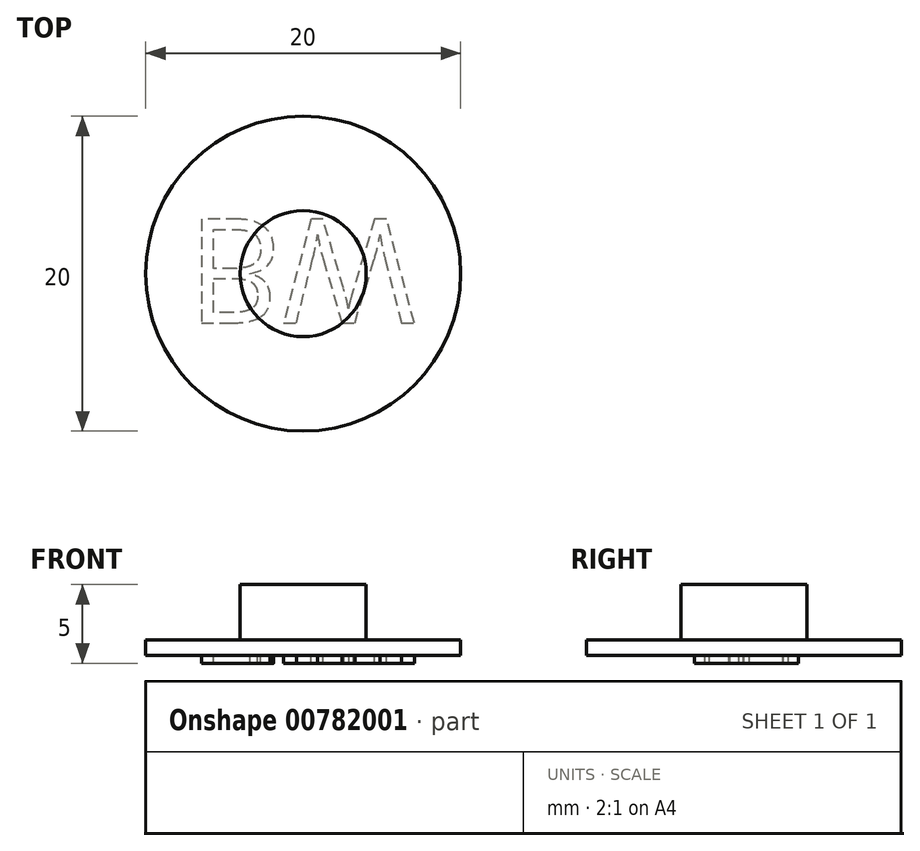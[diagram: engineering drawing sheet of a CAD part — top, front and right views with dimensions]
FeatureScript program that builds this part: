
annotation { "Feature Type Name" : "Feature", "Feature Type Description" : "" }
export const myFeature = defineFeature(function(context is Context, id is Id, definition is map)
    precondition{}
    {
        {
            var Q0;
            Q0=qCreatedBy(makeId("Top.planeOp"),FACE);
            var sketch = newSketch(context, id + "F0", { "sketchPlane" : qUnion([Q0])});
            skCircle(sketch, "E0", {"center": v(0, 0) * mm, "radius": 10 * mm});
            skSolve(sketch);
        }
        {
            var Q0;
            Q0=makeQuery(id+"F0.imprint","IMPRINT",FACE,{"disambiguationData":[TD([[makeQuery(id+"F0.imprint","IMPRINT",EDGE,{"derivedFrom":sQuery(id+"F0.wireOp",EDGE,"E0")}),1.0]])]});
            extrude(context, id + "F1", {"entities" : qUnion([Q0]), "depth" : 1 * mm, "offsetDistance" : 25.4 * mm});
        }
        {
            var Q0;
            Q0=makeQuery(id+"F1.opExtrude","CAP_FACE",FACE,{"disambiguationData":[OSD([sQuery(id+"F0.wireOp",EDGE,"E0")])],"isStart":false});
            var sketch = newSketch(context, id + "F2", { "sketchPlane" : qUnion([Q0])});
            skCircle(sketch, "E1", {"center": v(0, 0) * mm, "radius": 4 * mm});
            skSolve(sketch);
        }
        {
            var Q0;
            Q0 = qSketchRegion(id + "F2", true);
            extrude(context, id + "F3", {"entities" : qUnion([Q0]), "operationType" : NewBodyOperationType.ADD, "depth" : 3.5 * mm, "offsetDistance" : 25.4 * mm});
        }
        {
            var Q0;
            Q0=makeQuery(id+"F1.opExtrude","CAP_FACE",FACE,{"disambiguationData":[OSD([sQuery(id+"F0.wireOp",EDGE,"E0")])],"isStart":true});
            var sketch = newSketch(context, id + "F4", { "sketchPlane" : qUnion([Q0])});
            skText(sketch, "E2", { "text": "BW", "fontName": "OpenSans-Regular.ttf"});
            const initialGuessF4  = {"E2": [-0.00735, -0.00346, 1, 0, 0.00665]};
            skSetInitialGuess(sketch, initialGuessF4);
            skSolve(sketch);
        }
        {
            var Q0;
            Q0 = qSketchRegion(id + "F4", true);
            extrude(context, id + "F5", {"entities" : qUnion([Q0]), "operationType" : NewBodyOperationType.ADD, "depth" : 0.5 * mm, "offsetDistance" : 25.4 * mm});
        }
    });
